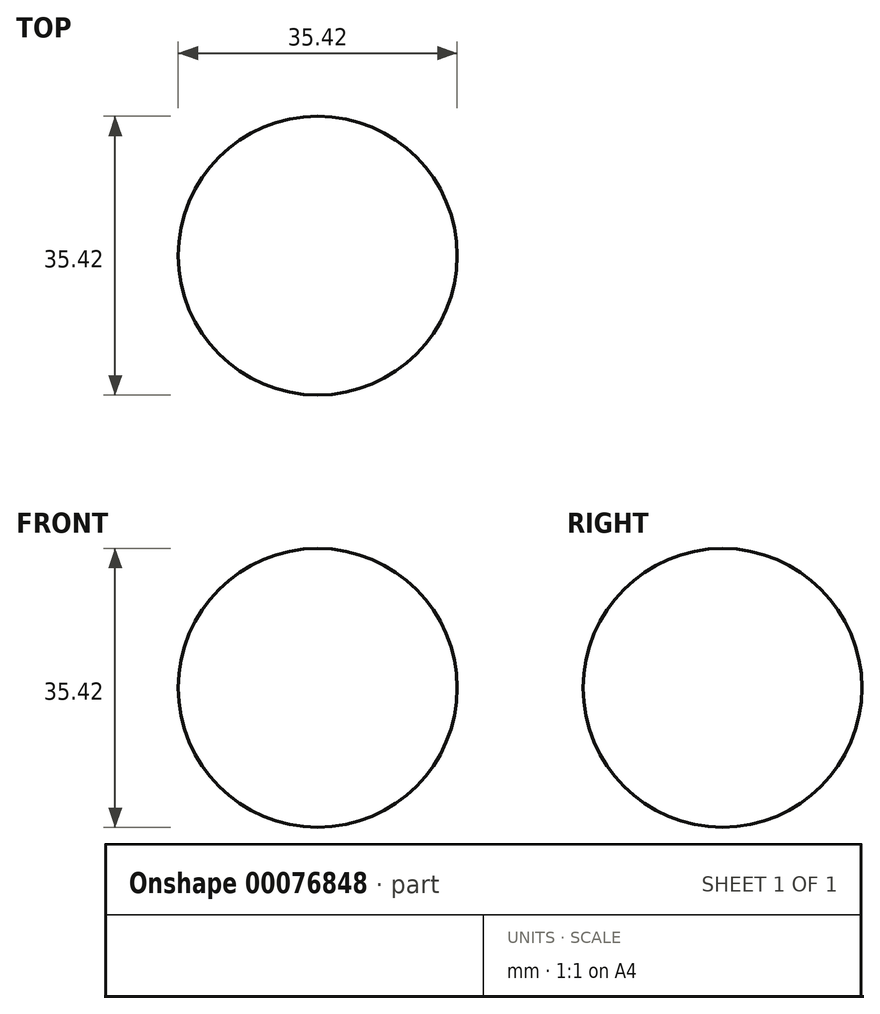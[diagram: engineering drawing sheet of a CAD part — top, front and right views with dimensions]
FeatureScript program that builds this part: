
annotation { "Feature Type Name" : "Feature", "Feature Type Description" : "" }
export const myFeature = defineFeature(function(context is Context, id is Id, definition is map)
    precondition{}
    {
        {
            var Q0;
            Q0=qCreatedBy(makeId("Front.planeOp"),FACE);
            var sketch = newSketch(context, id + "F0", { "sketchPlane" : qUnion([Q0])});
            skArc(sketch, "E0", {"start": v(0, 17.7) * mm, "mid": v(-17.7, 0) * mm, "end": v(0, -17.7) * mm});
            skLineSegment(sketch, "E1", {"start": v(0, 17.7) * mm, "end": v(0, -17.7) * mm});
            skSolve(sketch);
        }
        {
            var Q0;
            Q0=makeQuery(id+"F0.imprint","IMPRINT",FACE,{"disambiguationData":[TD([[makeQuery(id+"F0.imprint","IMPRINT",EDGE,{"derivedFrom":sQuery(id+"F0.wireOp",EDGE,"E0")}),1.0]])]});
            var Q1;
            Q1=sQuery(id+"F0.wireOp",EDGE,"E1");
            revolve(context, id + "F1", {"entities" : qUnion([Q0]), "axis" : qUnion([Q1]), "revolveType" : RevolveType.FULL});
        }
    });
